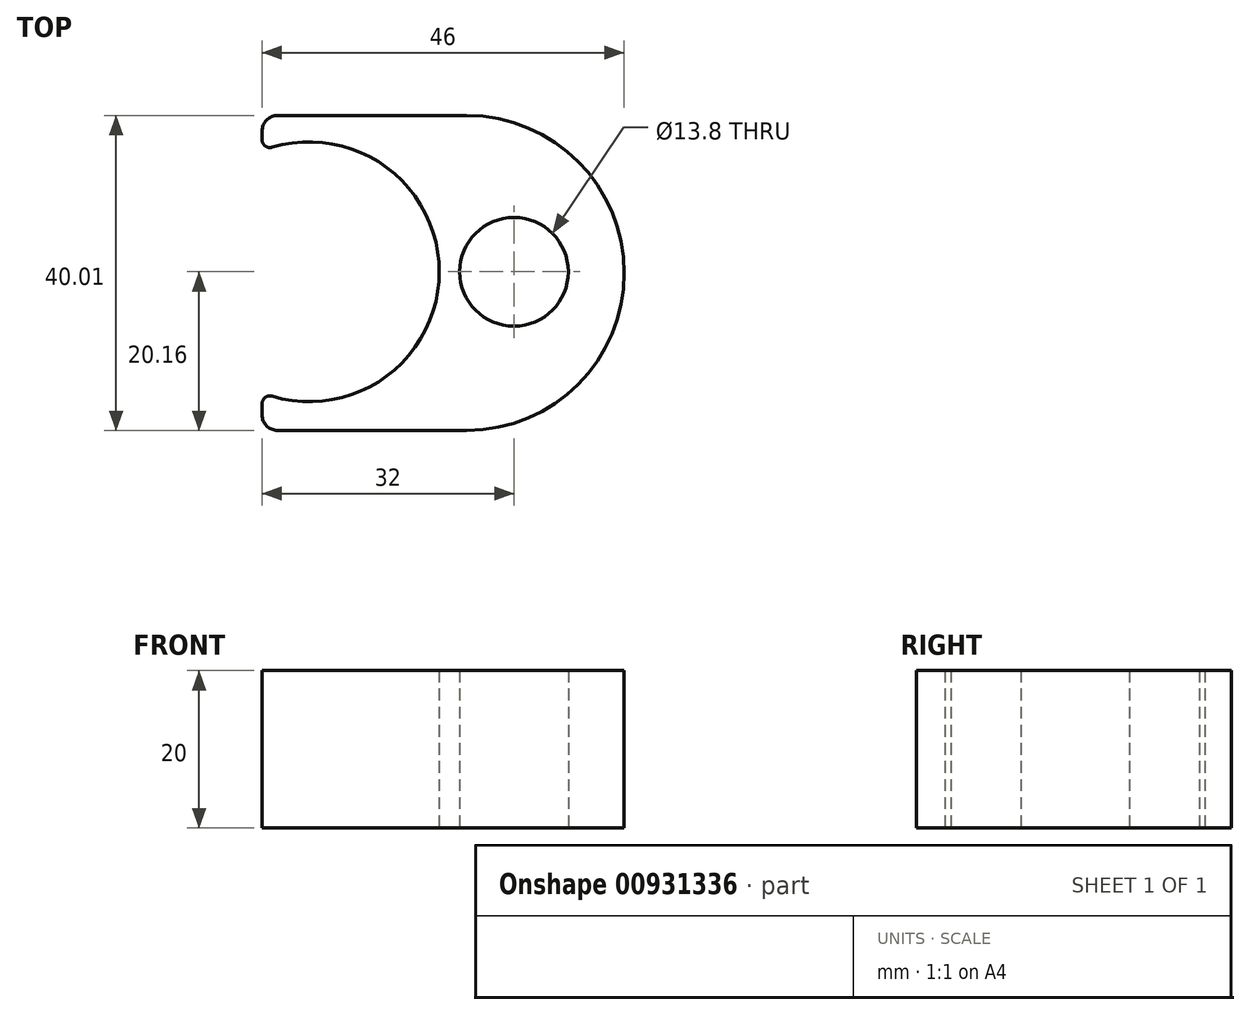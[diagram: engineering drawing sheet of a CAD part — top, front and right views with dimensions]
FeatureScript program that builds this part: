
annotation { "Feature Type Name" : "Feature", "Feature Type Description" : "" }
export const myFeature = defineFeature(function(context is Context, id is Id, definition is map)
    precondition{}
    {
        {
            var Q0;
            Q0=qCreatedBy(makeId("Top.planeOp"),FACE);
            var sketch = newSketch(context, id + "F0", { "sketchPlane" : qUnion([Q0])});
            skPoint(sketch, "E0.middle", {"position": v(0, 0) * mm});
            skCircle(sketch, "E1", {"center": v(26, 0) * mm, "radius": 6.9 * mm});
            skCircle(sketch, "E2", {"center": v(0, 0) * mm, "radius": 16.5 * mm});
            skLineSegment(sketch, "E3.left", {"start": v(-6, 19.85) * mm, "end": v(-6, -20.15) * mm});
            skLineSegment(sketch, "E4.bottom", {"start": v(-6, 19.85) * mm, "end": v(20, 19.85) * mm});
            skLineSegment(sketch, "E4.top", {"start": v(-6, -20.16) * mm, "end": v(20, -20.16) * mm});
            skLineSegment(sketch, "E4.left", {"start": v(-6, 19.85) * mm, "end": v(-6, -20.16) * mm});
            skArc(sketch, "E5", {"start": v(20, -20.16) * mm, "mid": v(40, -0.15) * mm, "end": v(20, 19.85) * mm});
            skSolve(sketch);
        }
        {
            var Q0;
            Q0=makeQuery(id+"F0.imprint","IMPRINT",FACE,{"disambiguationData":[TD([[makeQuery(id+"F0.imprint","IMPRINT",EDGE,{"derivedFrom":sQuery(id+"F0.wireOp",EDGE,"E1")}),-1.0]])]});
            extrude(context, id + "F1", {"entities" : qUnion([Q0]), "depth" : 20 * mm, "offsetDistance" : 25 * mm});
        }
        {
            var Q0;
            {var subQ0=sQuery(id+"F0.wireOp",EDGE,"te4v7hS6-debc-boBF-J155-MMZKSzko7mBj");var subQ1=sQuery(id+"F0.wireOp",EDGE,"E3.left");Q0=makeQuery(id+"F1.opExtrude","SWEPT_EDGE",EDGE,{"disambiguationData":[OSD([subQ1,subQ0]),TDD([makeQuery(id+"F0.imprint","INTERSECT",VERTEX,{"disambiguationData":[OD(1.0)],"derivedFrom":[subQ1,subQ0]})])]});}
            var Q1;
            {var subQ0=sQuery(id+"F0.wireOp",EDGE,"te4v7hS6-debc-boBF-J155-MMZKSzko7mBj");var subQ1=sQuery(id+"F0.wireOp",EDGE,"E3.left");Q1=makeQuery(id+"F1.opExtrude","SWEPT_EDGE",EDGE,{"disambiguationData":[OSD([subQ1,subQ0]),TDD([makeQuery(id+"F0.imprint","INTERSECT",VERTEX,{"disambiguationData":[OD(0.0)],"derivedFrom":[subQ1,subQ0]})])]});}
            fillet(context, id + "F2", {"entities" : qUnion([Q0, Q1]), "radius" : 1 * mm, "tangentPropagation" : true, "allowEdgeOverflow" : false});
        }
        {
            var Q0;
            Q0=makeQuery(id+"F1.opExtrude","SWEPT_EDGE",EDGE,{"disambiguationData":[OSD([sQuery(id+"F0.wireOp",EDGE,"E4.top"),sQuery(id+"F0.wireOp",EDGE,"E4.left")])]});
            var Q1;
            Q1=makeQuery(id+"F1.opExtrude","SWEPT_EDGE",EDGE,{"disambiguationData":[OSD([sQuery(id+"F0.wireOp",EDGE,"E4.bottom"),sQuery(id+"F0.wireOp",EDGE,"E4.left")])]});
            fillet(context, id + "F3", {"entities" : qUnion([Q0, Q1]), "radius" : 2 * mm, "tangentPropagation" : true, "allowEdgeOverflow" : false});
        }
    });
